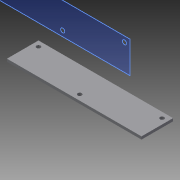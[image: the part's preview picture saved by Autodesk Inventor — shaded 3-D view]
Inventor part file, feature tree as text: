
AUTODESK INVENTOR PART (.ipt)
format: ipt  version: 2015 (Build 190159000, 159)  size: 84,480 bytes
history: native  units: mm
features: extrude x1, sketch x1
ambient origin geometry x8: Origin, YZ Plane, XZ Plane, XY Plane, X Axis, Y Axis, Z Axis, Center Point
bodies: Solid1 (feature_tree)
feature tree (2):
  extrude  "Extrusion1"  Depth=23.0mm
  sketch  "Sketch1"  dims[d0=98.0mm d1=23.0mm d2=4.0mm d3=4.0mm d4=3.0mm d5=4.0mm d6=4.0mm d7=3.0mm d8=4.0mm d9=3.0mm d10=2.0mm d11=0.0mm]
